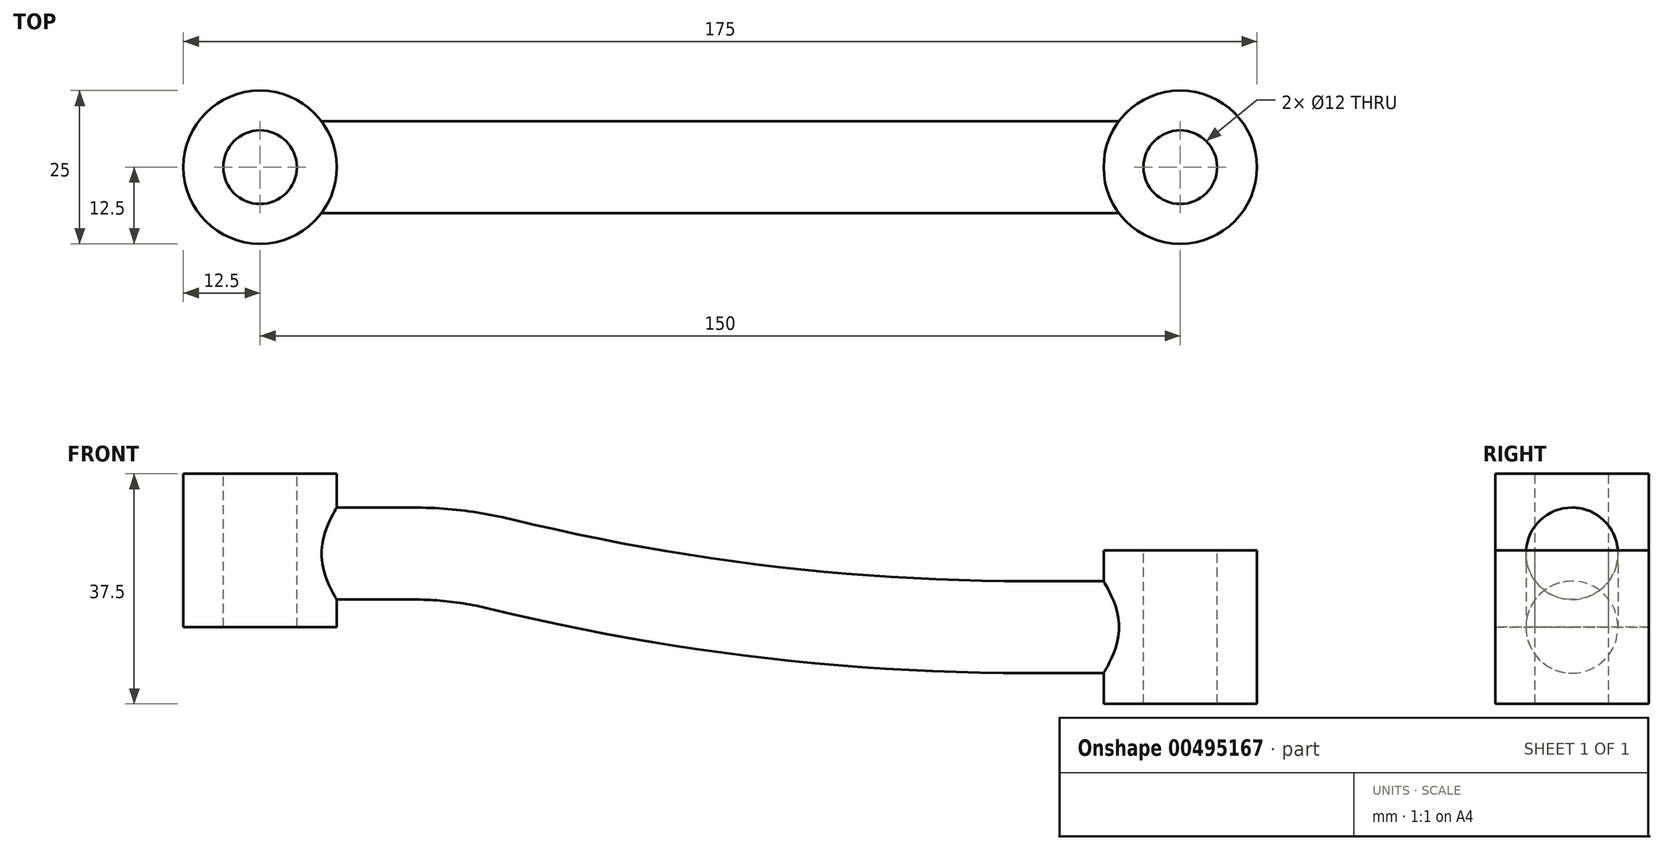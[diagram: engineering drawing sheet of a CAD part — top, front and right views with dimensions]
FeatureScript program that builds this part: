
annotation { "Feature Type Name" : "Feature", "Feature Type Description" : "" }
export const myFeature = defineFeature(function(context is Context, id is Id, definition is map)
    precondition{}
    {
        {
            var Q0;
            Q0=qCreatedBy(makeId("Top.planeOp"),FACE);
            var sketch = newSketch(context, id + "F0", { "sketchPlane" : qUnion([Q0])});
            skCircle(sketch, "E0", {"center": v(0, 0) * mm, "radius": 12.5 * mm});
            skCircle(sketch, "E1", {"center": v(150, 0) * mm, "radius": 12.5 * mm});
            skSolve(sketch);
        }
        {
            var Q0;
            Q0=makeQuery(id+"F0.imprint","IMPRINT",FACE,{"disambiguationData":[TD([[makeQuery(id+"F0.imprint","IMPRINT",EDGE,{"derivedFrom":sQuery(id+"F0.wireOp",EDGE,"E0")}),1.0]])]});
            extrude(context, id + "F1", {"entities" : qUnion([Q0]), "depth" : 25 * mm});
        }
        {
            var Q0;
            Q0=makeQuery(id+"F0.imprint","IMPRINT",FACE,{"disambiguationData":[TD([[makeQuery(id+"F0.imprint","IMPRINT",EDGE,{"derivedFrom":sQuery(id+"F0.wireOp",EDGE,"E1")}),1.0]])]});
            extrude(context, id + "F2", {"entities" : qUnion([Q0]), "endBound" : BoundingType.SYMMETRIC, "depth" : 25 * mm});
        }
        {
            var Q0;
            Q0=qCreatedBy(makeId("Front.planeOp"),FACE);
            var sketch = newSketch(context, id + "F3", { "sketchPlane" : qUnion([Q0])});
            skLineSegment(sketch, "E2", {"start": v(0, 12) * mm, "end": v(25, 12) * mm});
            skArc(sketch, "E3", {"start": v(25, 12) * mm, "mid": v(32.15, 11.57) * mm, "end": v(39.2, 10.3) * mm});
            skArc(sketch, "E4", {"start": v(39.2, 10.3) * mm, "mid": v(81.79, 2.58) * mm, "end": v(125, 0) * mm});
            skLineSegment(sketch, "E5", {"start": v(125, 0) * mm, "end": v(150, 0) * mm});
            skSolve(sketch);
        }
        {
            var Q0;
            Q0=qCreatedBy(makeId("Right.planeOp"),FACE);
            var sketch = newSketch(context, id + "F4", { "sketchPlane" : qUnion([Q0])});
            skCircle(sketch, "E6", {"center": v(0, 12) * mm, "radius": 7.5 * mm});
            skSolve(sketch);
        }
        {
            var Q0;
            Q0 = qSketchRegion(id + "F4", true);
            var Q1;
            Q1=sQuery(id+"F3.wireOp",EDGE,"E2");
            var Q2;
            Q2=sQuery(id+"F3.wireOp",EDGE,"E3");
            var Q3;
            Q3=sQuery(id+"F3.wireOp",EDGE,"E4");
            var Q4;
            Q4=sQuery(id+"F3.wireOp",EDGE,"E5");
            sweep(context, id + "F5", {"operationType" : NewBodyOperationType.ADD, "profiles" : qUnion([Q0]), "path" : qUnion([Q1, Q2, Q3, Q4])});
        }
        {
            var Q0;
            Q0=makeQuery(id+"F1.opExtrude","CAP_FACE",FACE,{"disambiguationData":[OSD([sQuery(id+"F0.wireOp",EDGE,"E0")])],"isStart":false});
            var sketch = newSketch(context, id + "F6", { "sketchPlane" : qUnion([Q0])});
            skCircle(sketch, "E7", {"center": v(0, 0) * mm, "radius": 6 * mm});
            skCircle(sketch, "E8", {"center": v(150, 0) * mm, "radius": 6 * mm});
            skSolve(sketch);
        }
        {
            var Q0;
            Q0=makeQuery(id+"F6.imprint","IMPRINT",FACE,{"disambiguationData":[TD([[makeQuery(id+"F6.imprint","IMPRINT",EDGE,{"derivedFrom":sQuery(id+"F6.wireOp",EDGE,"E7")}),1.0]])]});
            var Q1;
            Q1=makeQuery(id+"F6.imprint","IMPRINT",FACE,{"disambiguationData":[TD([[makeQuery(id+"F6.imprint","IMPRINT",EDGE,{"derivedFrom":sQuery(id+"F6.wireOp",EDGE,"E8")}),1.0]])]});
            extrude(context, id + "F7", {"entities" : qUnion([Q0, Q1]), "operationType" : NewBodyOperationType.REMOVE, "endBound" : BoundingType.THROUGH_ALL, "oppositeDirection" : true, "depth" : 25.4 * mm});
        }
    });
